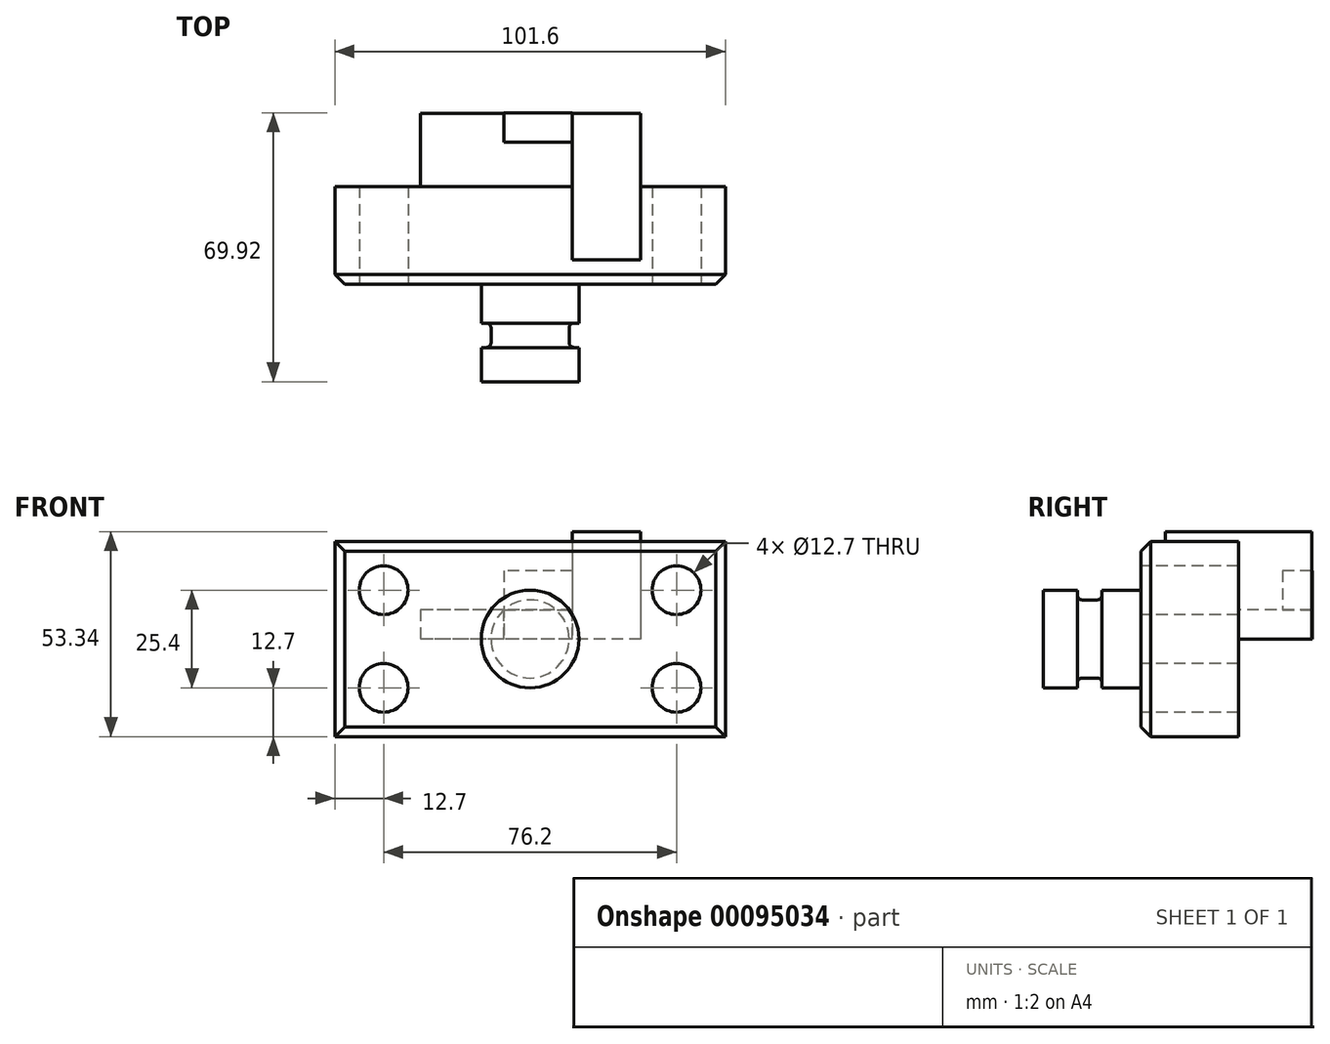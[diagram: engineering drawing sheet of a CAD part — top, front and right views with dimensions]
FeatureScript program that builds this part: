
annotation { "Feature Type Name" : "Feature", "Feature Type Description" : "" }
export const myFeature = defineFeature(function(context is Context, id is Id, definition is map)
    precondition{}
    {
        {
            var Q0;
            Q0=qCreatedBy(makeId("Front.planeOp"),FACE);
            var sketch = newSketch(context, id + "F0", { "sketchPlane" : qUnion([Q0])});
            skLineSegment(sketch, "E0.bottom", {"start": v(-50.8, -25.4) * mm, "end": v(50.8, -25.4) * mm});
            skLineSegment(sketch, "E0.top", {"start": v(-50.8, 25.4) * mm, "end": v(50.8, 25.4) * mm});
            skLineSegment(sketch, "E0.left", {"start": v(-50.8, -25.4) * mm, "end": v(-50.8, 25.4) * mm});
            skLineSegment(sketch, "E0.right", {"start": v(50.8, -25.4) * mm, "end": v(50.8, 25.4) * mm});
            skPoint(sketch, "E0.middle", {"position": v(0, 0) * mm});
            skSolve(sketch);
        }
        {
            var Q0;
            Q0=makeQuery(id+"F0.imprint","IMPRINT",FACE,{"disambiguationData":[TD([[makeQuery(id+"F0.imprint","IMPRINT",EDGE,{"derivedFrom":sQuery(id+"F0.wireOp",EDGE,"E0.bottom")}),1.0]])]});
            extrude(context, id + "F1", {"entities" : qUnion([Q0]), "depth" : 25.4 * mm});
        }
        {
            var Q0;
            Q0=makeQuery(id+"F1.opExtrude","CAP_FACE",FACE,{"disambiguationData":[OSD([sQuery(id+"F0.wireOp",EDGE,"E0.bottom"),sQuery(id+"F0.wireOp",EDGE,"E0.top"),sQuery(id+"F0.wireOp",EDGE,"E0.left"),sQuery(id+"F0.wireOp",EDGE,"E0.right")])],"isStart":false});
            var sketch = newSketch(context, id + "F2", { "sketchPlane" : qUnion([Q0])});
            skCircle(sketch, "E1", {"center": v(-38.1, 12.7) * mm, "radius": 6.35 * mm});
            skCircle(sketch, "E2", {"center": v(-38.1, -12.7) * mm, "radius": 6.35 * mm});
            skCircle(sketch, "E3", {"center": v(38.1, 12.7) * mm, "radius": 6.35 * mm});
            skCircle(sketch, "E4", {"center": v(38.1, -12.7) * mm, "radius": 6.35 * mm});
            skSolve(sketch);
        }
        {
            var Q0;
            Q0 = qSketchRegion(id + "F2", true);
            extrude(context, id + "F3", {"entities" : qUnion([Q0]), "operationType" : NewBodyOperationType.REMOVE, "endBound" : BoundingType.THROUGH_ALL, "oppositeDirection" : true, "depth" : 25.4 * mm});
        }
        {
            var Q0;
            Q0=qCreatedBy(makeId("Top.planeOp"),FACE);
            var sketch = newSketch(context, id + "F4", { "sketchPlane" : qUnion([Q0])});
            skLineSegment(sketch, "E5.bottom", {"start": v(-12.7, -25.4) * mm, "end": v(0, -25.4) * mm});
            skLineSegment(sketch, "E5.top", {"start": v(-12.7, -50.8) * mm, "end": v(0, -50.8) * mm});
            skLineSegment(sketch, "E5.left", {"start": v(0, -25.4) * mm, "end": v(0, -50.8) * mm});
            skLineSegment(sketch, "E5.right", {"start": v(-12.7, -25.4) * mm, "end": v(-12.7, -50.8) * mm});
            skSolve(sketch);
        }
        {
            var Q0;
            Q0 = qSketchRegion(id + "F4", true);
            var Q1;
            Q1=sQuery(id+"F4.wireOp",EDGE,"E5.left");
            revolve(context, id + "F5", {"operationType" : NewBodyOperationType.ADD, "entities" : qUnion([Q0]), "axis" : qUnion([Q1]), "revolveType" : RevolveType.FULL});
        }
        {
            var Q0;
            Q0=qCreatedBy(makeId("Top.planeOp"),FACE);
            var sketch = newSketch(context, id + "F6", { "sketchPlane" : qUnion([Q0])});
            skLineSegment(sketch, "E6.bottom", {"start": v(-15.96, -41.9) * mm, "end": v(-10.16, -41.9) * mm});
            skLineSegment(sketch, "E6.top", {"start": v(-15.96, -35.56) * mm, "end": v(-10.16, -35.56) * mm});
            skLineSegment(sketch, "E6.left", {"start": v(-15.96, -41.91) * mm, "end": v(-15.96, -35.56) * mm});
            skLineSegment(sketch, "E6.right", {"start": v(-10.16, -41.9) * mm, "end": v(-10.16, -35.56) * mm});
            skLineSegment(sketch, "E7", {"start": v(0, 0) * mm, "end": v(0, -18.05) * mm, "construction": true});
            skSolve(sketch);
        }
        {
            var Q0;
            Q0 = qSketchRegion(id + "F6", true);
            var Q1;
            Q1=sQuery(id+"F6.wireOp",EDGE,"E7");
            revolve(context, id + "F7", {"operationType" : NewBodyOperationType.REMOVE, "entities" : qUnion([Q0]), "axis" : qUnion([Q1]), "revolveType" : RevolveType.FULL, "oppositeDirection" : true});
        }
        {
            var Q0;
            Q0=makeQuery(id+"F5.opRevolve","SWEPT_EDGE",EDGE,{"disambiguationData":[OSD([sQuery(id+"F4.wireOp",EDGE,"E5.bottom"),sQuery(id+"F4.wireOp",EDGE,"E5.right")])]});
            var Q1;
            Q1=makeQuery(id+"F7.boolean.opBoolean","COPY",EDGE,{"derivedFrom":makeQuery(id+"F7.opRevolve","SWEPT_EDGE",EDGE,{"disambiguationData":[OSD([sQuery(id+"F6.wireOp",EDGE,"E6.bottom"),sQuery(id+"F6.wireOp",EDGE,"E6.right")])]})});
            var Q2;
            Q2=makeQuery(id+"F7.boolean.opBoolean","COPY",EDGE,{"derivedFrom":makeQuery(id+"F7.opRevolve","SWEPT_EDGE",EDGE,{"disambiguationData":[OSD([sQuery(id+"F6.wireOp",EDGE,"E6.top"),sQuery(id+"F6.wireOp",EDGE,"E6.right")])]})});
            fillet(context, id + "F8", {"entities" : qUnion([Q0, Q1, Q2]), "radius" : 1.27 * mm, "tangentPropagation" : true, "allowEdgeOverflow" : false});
        }
        {
            var Q0;
            Q0=makeQuery(id+"F1.opExtrude","CAP_EDGE",EDGE,{"disambiguationData":[OSD([sQuery(id+"F0.wireOp",EDGE,"E0.bottom")])],"isStart":false});
            var Q1;
            Q1=makeQuery(id+"F1.opExtrude","CAP_EDGE",EDGE,{"disambiguationData":[OSD([sQuery(id+"F0.wireOp",EDGE,"E0.left")])],"isStart":false});
            var Q2;
            Q2=makeQuery(id+"F1.opExtrude","CAP_EDGE",EDGE,{"disambiguationData":[OSD([sQuery(id+"F0.wireOp",EDGE,"E0.top")])],"isStart":false});
            var Q3;
            Q3=makeQuery(id+"F1.opExtrude","CAP_EDGE",EDGE,{"disambiguationData":[OSD([sQuery(id+"F0.wireOp",EDGE,"E0.right")])],"isStart":false});
            chamfer(context, id + "F9", {"entities" : qUnion([Q0, Q1, Q2, Q3]), "width" : 2.54 * mm, "tangentPropagation" : true});
        }
        {
            var Q0;
            Q0=qCreatedBy(makeId("Top.planeOp"),FACE);
            var sketch = newSketch(context, id + "F10", { "sketchPlane" : qUnion([Q0])});
            skLineSegment(sketch, "E8.bottom", {"start": v(28.57, 19.05) * mm, "end": v(-28.58, 19.05) * mm});
            skLineSegment(sketch, "E8.top", {"start": v(28.58, -19.05) * mm, "end": v(-28.57, -19.05) * mm});
            skLineSegment(sketch, "E8.left", {"start": v(28.57, 19.05) * mm, "end": v(28.58, -19.05) * mm});
            skLineSegment(sketch, "E8.right", {"start": v(-28.58, 19.05) * mm, "end": v(-28.57, -19.05) * mm});
            skPoint(sketch, "E8.middle", {"position": v(0, 0) * mm});
            skSolve(sketch);
        }
        {
            var Q0;
            Q0 = qSketchRegion(id + "F10", true);
            extrude(context, id + "F11", {"entities" : qUnion([Q0]), "depth" : 7.62 * mm});
        }
        {
            var Q0;
            Q0=qCreatedBy(makeId("Top.planeOp"),FACE);
            var sketch = newSketch(context, id + "F12", { "sketchPlane" : qUnion([Q0])});
            skLineSegment(sketch, "E9.bottom", {"start": v(28.8, -19.05) * mm, "end": v(11.02, -19.05) * mm});
            skLineSegment(sketch, "E9.top", {"start": v(28.8, 19.05) * mm, "end": v(11.02, 19.05) * mm});
            skLineSegment(sketch, "E9.left", {"start": v(28.8, -19.05) * mm, "end": v(28.8, 19.05) * mm});
            skLineSegment(sketch, "E9.right", {"start": v(11.02, -19.05) * mm, "end": v(11.02, 19.05) * mm});
            skSolve(sketch);
        }
        {
            var Q0;
            Q0=makeQuery(id+"F12.imprint","IMPRINT",FACE,{"disambiguationData":[TD([[makeQuery(id+"F12.imprint","IMPRINT",EDGE,{"derivedFrom":sQuery(id+"F12.wireOp",EDGE,"E9.bottom")}),-1.0]])]});
            extrude(context, id + "F13", {"entities" : qUnion([Q0]), "operationType" : NewBodyOperationType.ADD, "depth" : 27.94 * mm});
        }
        {
            var Q0;
            Q0=qCreatedBy(makeId("Top.planeOp"),FACE);
            var sketch = newSketch(context, id + "F14", { "sketchPlane" : qUnion([Q0])});
            skLineSegment(sketch, "E10.bottom", {"start": v(10.98, 19.12) * mm, "end": v(-6.8, 19.12) * mm});
            skLineSegment(sketch, "E10.top", {"start": v(10.98, 11.5) * mm, "end": v(-6.8, 11.5) * mm});
            skLineSegment(sketch, "E10.left", {"start": v(10.98, 19.12) * mm, "end": v(10.98, 11.5) * mm});
            skLineSegment(sketch, "E10.right", {"start": v(-6.8, 19.12) * mm, "end": v(-6.8, 11.5) * mm});
            skLineSegment(sketch, "E11.bottom", {"start": v(10.85, -18.99) * mm, "end": v(-6.93, -18.99) * mm});
            skLineSegment(sketch, "E11.top", {"start": v(10.85, -11.37) * mm, "end": v(-6.93, -11.37) * mm});
            skLineSegment(sketch, "E11.left", {"start": v(10.85, -18.99) * mm, "end": v(10.85, -11.37) * mm});
            skLineSegment(sketch, "E11.right", {"start": v(-6.93, -18.99) * mm, "end": v(-6.93, -11.37) * mm});
            skSolve(sketch);
        }
        {
            var Q0;
            Q0 = qSketchRegion(id + "F14", true);
            extrude(context, id + "F15", {"entities" : qUnion([Q0]), "operationType" : NewBodyOperationType.ADD, "depth" : 17.78 * mm});
        }
    });
